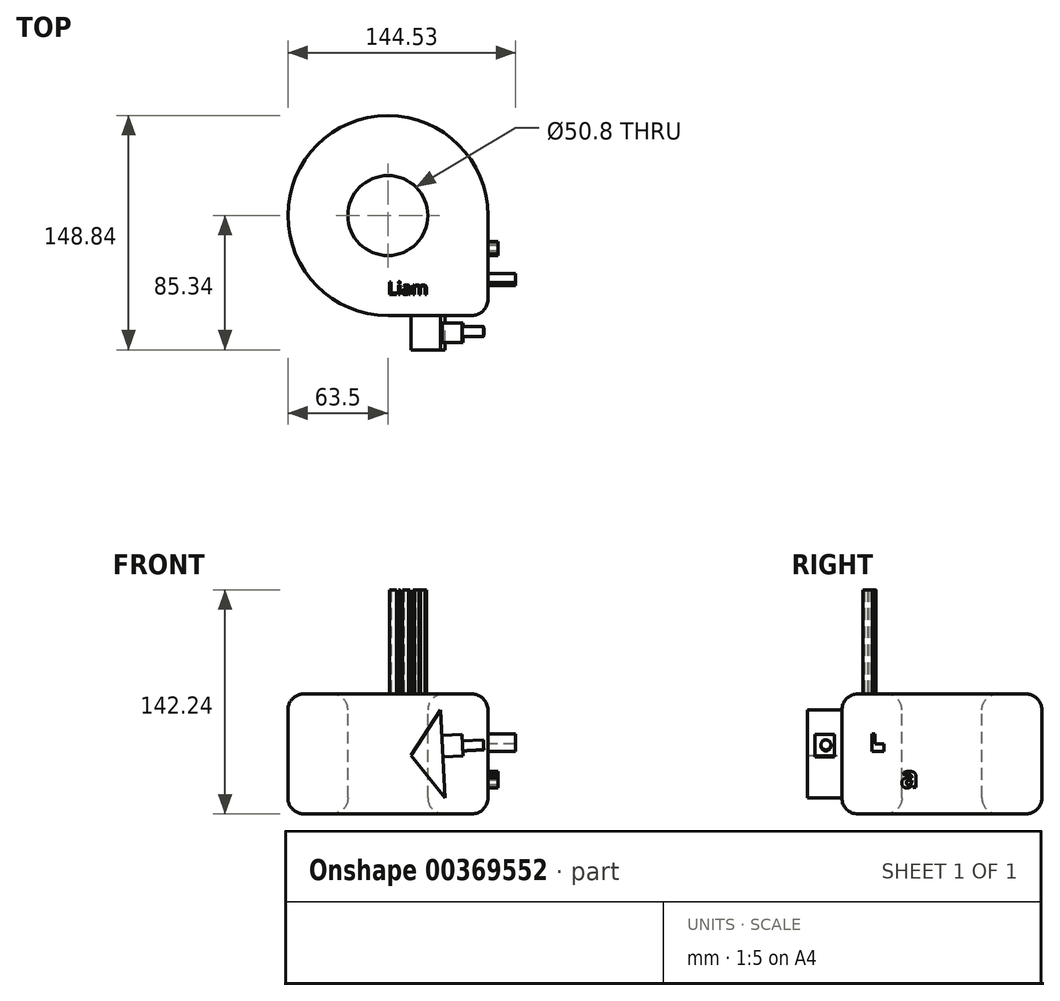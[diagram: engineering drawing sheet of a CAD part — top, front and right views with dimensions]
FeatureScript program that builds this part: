
annotation { "Feature Type Name" : "Feature", "Feature Type Description" : "" }
export const myFeature = defineFeature(function(context is Context, id is Id, definition is map)
    precondition{}
    {
        {
            var Q0;
            Q0=qCreatedBy(makeId("Top.planeOp"),FACE);
            var sketch = newSketch(context, id + "F0", { "sketchPlane" : qUnion([Q0])});
            skLineSegment(sketch, "E0.bottom", {"start": v(63.5, 63.5) * mm, "end": v(-63.5, 63.5) * mm});
            skLineSegment(sketch, "E0.top", {"start": v(63.5, -63.5) * mm, "end": v(-63.5, -63.5) * mm});
            skLineSegment(sketch, "E0.left", {"start": v(63.5, 63.5) * mm, "end": v(63.5, -63.5) * mm});
            skLineSegment(sketch, "E0.right", {"start": v(-63.5, 63.5) * mm, "end": v(-63.5, -63.5) * mm});
            skPoint(sketch, "E0.middle", {"position": v(0, 0) * mm});
            skSolve(sketch);
        }
        {
            var Q0;
            Q0=makeQuery(id+"F0.imprint","IMPRINT",FACE,{"disambiguationData":[TD([[makeQuery(id+"F0.imprint","IMPRINT",EDGE,{"derivedFrom":sQuery(id+"F0.wireOp",EDGE,"E0.bottom")}),1.0]])]});
            extrude(context, id + "F1", {"entities" : qUnion([Q0]), "depth" : 76.2 * mm});
        }
        {
            var Q0;
            Q0=makeQuery(id+"F1.opExtrude","CAP_FACE",FACE,{"disambiguationData":[OSD([sQuery(id+"F0.wireOp",EDGE,"E0.bottom"),sQuery(id+"F0.wireOp",EDGE,"E0.top"),sQuery(id+"F0.wireOp",EDGE,"E0.left"),sQuery(id+"F0.wireOp",EDGE,"E0.right")])],"isStart":false});
            var sketch = newSketch(context, id + "F2", { "sketchPlane" : qUnion([Q0])});
            skCircle(sketch, "E1", {"center": v(0, 0) * mm, "radius": 63.5 * mm});
            skSolve(sketch);
        }
        {
            var Q0;
            {var subQ0=sQuery(id+"F2.wireOp",EDGE,"E1");var subQ1=makeQuery(id+"F1.opExtrude","CAP_EDGE",EDGE,{"disambiguationData":[OSD([sQuery(id+"F0.wireOp",EDGE,"E0.bottom")])],"isStart":false});var subQ2=makeQuery(id+"F2.imprint","INTERSECT",VERTEX,{"derivedFrom":[subQ1,subQ0]});Q0=makeQuery(id+"F2.imprint","IMPRINT",FACE,{"disambiguationData":[TD([[makeQuery(id+"F2.imprint","IMPRINT",EDGE,{"disambiguationData":[TD([[subQ2,1.0]])],"derivedFrom":subQ0}),-1.0]])]});}
            var Q1;
            {var subQ0=sQuery(id+"F2.wireOp",EDGE,"E1");var subQ1=makeQuery(id+"F1.opExtrude","CAP_EDGE",EDGE,{"disambiguationData":[OSD([sQuery(id+"F0.wireOp",EDGE,"E0.bottom")])],"isStart":false});var subQ2=makeQuery(id+"F2.imprint","INTERSECT",VERTEX,{"derivedFrom":[subQ1,subQ0]});Q1=makeQuery(id+"F2.imprint","IMPRINT",FACE,{"disambiguationData":[TD([[makeQuery(id+"F2.imprint","IMPRINT",EDGE,{"disambiguationData":[TD([[subQ2,-1.0]])],"derivedFrom":subQ0}),-1.0]])]});}
            extrude(context, id + "F3", {"entities" : qUnion([Q0, Q1]), "operationType" : NewBodyOperationType.REMOVE, "oppositeDirection" : true, "depth" : 84.58 * mm});
        }
        {
            var Q0;
            Q0=makeQuery(id+"F1.opExtrude","SWEPT_EDGE",EDGE,{"disambiguationData":[OSD([sQuery(id+"F0.wireOp",EDGE,"E0.top"),sQuery(id+"F0.wireOp",EDGE,"E0.right")])]});
            fillet(context, id + "F4", {"entities" : qUnion([Q0]), "radius" : 63.5 * mm, "tangentPropagation" : true, "allowEdgeOverflow" : false});
        }
        {
            var Q0;
            Q0=makeQuery(id+"F1.opExtrude","CAP_FACE",FACE,{"disambiguationData":[OSD([sQuery(id+"F0.wireOp",EDGE,"E0.bottom"),sQuery(id+"F0.wireOp",EDGE,"E0.top"),sQuery(id+"F0.wireOp",EDGE,"E0.left"),sQuery(id+"F0.wireOp",EDGE,"E0.right")])],"isStart":false});
            var sketch = newSketch(context, id + "F5", { "sketchPlane" : qUnion([Q0])});
            skCircle(sketch, "E2", {"center": v(0, 0) * mm, "radius": 25.4 * mm});
            skSolve(sketch);
        }
        {
            var Q0;
            Q0=makeQuery(id+"F5.imprint","IMPRINT",FACE,{"disambiguationData":[TD([[makeQuery(id+"F5.imprint","IMPRINT",EDGE,{"derivedFrom":sQuery(id+"F5.wireOp",EDGE,"E2")}),1.0]])]});
            extrude(context, id + "F6", {"entities" : qUnion([Q0]), "operationType" : NewBodyOperationType.REMOVE, "oppositeDirection" : true, "depth" : 85.1 * mm});
        }
        {
            var Q0;
            Q0=makeQuery(id+"F1.opExtrude","SWEPT_FACE",FACE,{"disambiguationData":[OSD([sQuery(id+"F0.wireOp",EDGE,"E0.left")])]});
            var Q1;
            Q1=makeQuery(id+"F1.opExtrude","SWEPT_FACE",FACE,{"disambiguationData":[OSD([sQuery(id+"F0.wireOp",EDGE,"E0.top")])]});
            var Q2;
            Q2=makeQuery(id+"F6.boolean.opBoolean","COPY",FACE,{"derivedFrom":makeQuery(id+"F6.opExtrude","SWEPT_FACE",FACE,{"disambiguationData":[OSD([sQuery(id+"F5.wireOp",EDGE,"E2")])]})});
            fillet(context, id + "F7", {"entities" : qUnion([Q0, Q1, Q2]), "radius" : 10.16 * mm, "tangentPropagation" : true, "allowEdgeOverflow" : false});
        }
        {
            var Q0;
            Q0=makeQuery(id+"F1.opExtrude","SWEPT_FACE",FACE,{"disambiguationData":[OSD([sQuery(id+"F0.wireOp",EDGE,"E0.top")])]});
            var sketch = newSketch(context, id + "F8", { "sketchPlane" : qUnion([Q0])});
            skLineSegment(sketch, "E3", {"start": v(14.58, 37.22) * mm, "end": v(36.4, 10.16) * mm});
            skLineSegment(sketch, "E4", {"start": v(14.58, 37.22) * mm, "end": v(33.36, 66.04) * mm});
            skLineSegment(sketch, "E5", {"start": v(33.36, 66.04) * mm, "end": v(36.4, 10.16) * mm});
            skSolve(sketch);
        }
        {
            var Q0;
            Q0=makeQuery(id+"F8.imprint","IMPRINT",FACE,{"disambiguationData":[TD([[makeQuery(id+"F8.imprint","IMPRINT",EDGE,{"derivedFrom":sQuery(id+"F8.wireOp",EDGE,"E3")}),1.0]])]});
            extrude(context, id + "F9", {"entities" : qUnion([Q0]), "operationType" : NewBodyOperationType.ADD, "depth" : 21.84 * mm});
        }
        {
            var Q0;
            Q0=makeQuery(id+"F9.opExtrude","SWEPT_FACE",FACE,{"disambiguationData":[OSD([sQuery(id+"F8.wireOp",EDGE,"E5")])]});
            var sketch = newSketch(context, id + "F10", { "sketchPlane" : qUnion([Q0])});
            skLineSegment(sketch, "E6.bottom", {"start": v(-68.17, 34.13) * mm, "end": v(-80.67, 34.13) * mm});
            skLineSegment(sketch, "E6.top", {"start": v(-68.17, 47.87) * mm, "end": v(-80.67, 47.87) * mm});
            skLineSegment(sketch, "E6.left", {"start": v(-68.17, 34.13) * mm, "end": v(-68.17, 47.87) * mm});
            skLineSegment(sketch, "E6.right", {"start": v(-80.67, 34.13) * mm, "end": v(-80.67, 47.87) * mm});
            skPoint(sketch, "E6.middle", {"position": v(-74.42, 41) * mm});
            skPoint(sketch, "E6.middle.positionSnap0", {"position": v(-74.42, 64.13) * mm});
            skPoint(sketch, "E6.centerSnap0", {"position": v(-74.42, 64.13) * mm});
            skSolve(sketch);
        }
        {
            var Q0;
            Q0 = qSketchRegion(id + "F10", true);
            extrude(context, id + "F11", {"entities" : qUnion([Q0]), "operationType" : NewBodyOperationType.ADD, "depth" : 12.7 * mm});
        }
        {
            var Q0;
            Q0=makeQuery(id+"F11.opExtrude","CAP_FACE",FACE,{"disambiguationData":[OSD([sQuery(id+"F10.wireOp",EDGE,"E6.bottom"),sQuery(id+"F10.wireOp",EDGE,"E6.top"),sQuery(id+"F10.wireOp",EDGE,"E6.left"),sQuery(id+"F10.wireOp",EDGE,"E6.right")])],"isStart":false});
            var sketch = newSketch(context, id + "F12", { "sketchPlane" : qUnion([Q0])});
            skCircle(sketch, "E7", {"center": v(-73.66, 40.56) * mm, "radius": 3.15 * mm});
            skPoint(sketch, "E7.first.point", {"position": v(-73.87, 43.7) * mm});
            skPoint(sketch, "E7.second.point", {"position": v(-74.42, 37.5) * mm});
            skPoint(sketch, "E7.second.point.positionSnap0", {"position": v(-74.42, 34.13) * mm});
            skPoint(sketch, "E7.third.point", {"position": v(-76.78, 41) * mm});
            skPoint(sketch, "E7.third.point.positionSnap0", {"position": v(-80.67, 41) * mm});
            skSolve(sketch);
        }
        {
            var Q0;
            Q0=makeQuery(id+"F12.imprint","IMPRINT",FACE,{"disambiguationData":[TD([[makeQuery(id+"F12.imprint","IMPRINT",EDGE,{"derivedFrom":sQuery(id+"F12.wireOp",EDGE,"E7")}),1.0]])]});
            extrude(context, id + "F13", {"entities" : qUnion([Q0]), "operationType" : NewBodyOperationType.ADD, "depth" : 13.46 * mm});
        }
        {
            var Q0;
            Q0=makeQuery(id+"F1.opExtrude","SWEPT_FACE",FACE,{"disambiguationData":[OSD([sQuery(id+"F0.wireOp",EDGE,"E0.left")])]});
            var sketch = newSketch(context, id + "F14", { "sketchPlane" : qUnion([Q0])});
            skLineSegment(sketch, "E8", {"start": v(-44.56, 50.96) * mm, "end": v(-44.56, 39.67) * mm});
            skLineSegment(sketch, "E9", {"start": v(-44.56, 39.67) * mm, "end": v(-36.7, 39.67) * mm});
            skLineSegment(sketch, "E10", {"start": v(-36.7, 39.67) * mm, "end": v(-36.7, 44.58) * mm});
            skLineSegment(sketch, "E11", {"start": v(-36.7, 44.58) * mm, "end": v(-42.45, 44.58) * mm});
            skLineSegment(sketch, "E12", {"start": v(-42.45, 44.58) * mm, "end": v(-42.45, 50.96) * mm});
            skLineSegment(sketch, "E13", {"start": v(-44.56, 50.96) * mm, "end": v(-42.45, 50.96) * mm});
            skSolve(sketch);
        }
        {
            var Q0;
            Q0=makeQuery(id+"F14.imprint","IMPRINT",FACE,{"disambiguationData":[TD([[makeQuery(id+"F14.imprint","IMPRINT",EDGE,{"derivedFrom":sQuery(id+"F14.wireOp",EDGE,"E8")}),1.0]])]});
            extrude(context, id + "F15", {"entities" : qUnion([Q0]), "operationType" : NewBodyOperationType.ADD, "depth" : 17.53 * mm});
        }
        {
            var Q0;
            Q0=makeQuery(id+"F1.opExtrude","SWEPT_FACE",FACE,{"disambiguationData":[OSD([sQuery(id+"F0.wireOp",EDGE,"E0.left")])]});
            var sketch = newSketch(context, id + "F16", { "sketchPlane" : qUnion([Q0])});
            skText(sketch, "E14", { "text": "Liam ", "fontName": "OpenSans-Bold.ttf"});
            const initialGuessF16  = {"E14": [-0.0425, 0.0167, 1, 0, 0.01343]};
            skSetInitialGuess(sketch, initialGuessF16);
            skSolve(sketch);
        }
        {
            var Q0;
            Q0=makeQuery(id+"F16.imprint","IMPRINT",FACE,{"disambiguationData":[TD([[makeQuery(id+"F16.imprint","IMPRINT",EDGE,{"derivedFrom":sQuery(id+"F16.wireOp",EDGE,"E14.sketch_text.stroke-15")}),-1.0]])]});
            extrude(context, id + "F17", {"entities" : qUnion([Q0]), "operationType" : NewBodyOperationType.ADD, "depth" : 6.35 * mm});
        }
        {
            var Q0;
            Q0=makeQuery(id+"F1.opExtrude","CAP_FACE",FACE,{"disambiguationData":[OSD([sQuery(id+"F0.wireOp",EDGE,"E0.bottom"),sQuery(id+"F0.wireOp",EDGE,"E0.top"),sQuery(id+"F0.wireOp",EDGE,"E0.left"),sQuery(id+"F0.wireOp",EDGE,"E0.right")])],"isStart":false});
            var sketch = newSketch(context, id + "F18", { "sketchPlane" : qUnion([Q0])});
            skText(sketch, "E15", { "text": "Liam\n", "fontName": "OpenSans-Regular.ttf"});
            const initialGuessF18  = {"E15": [0, -0.05014, 1, 0, 0.0081]};
            skSetInitialGuess(sketch, initialGuessF18);
            skSolve(sketch);
        }
        {
            var Q0;
            Q0 = qSketchRegion(id + "F18", true);
            extrude(context, id + "F19", {"entities" : qUnion([Q0]), "operationType" : NewBodyOperationType.ADD, "depth" : 66.04 * mm});
        }
    });
